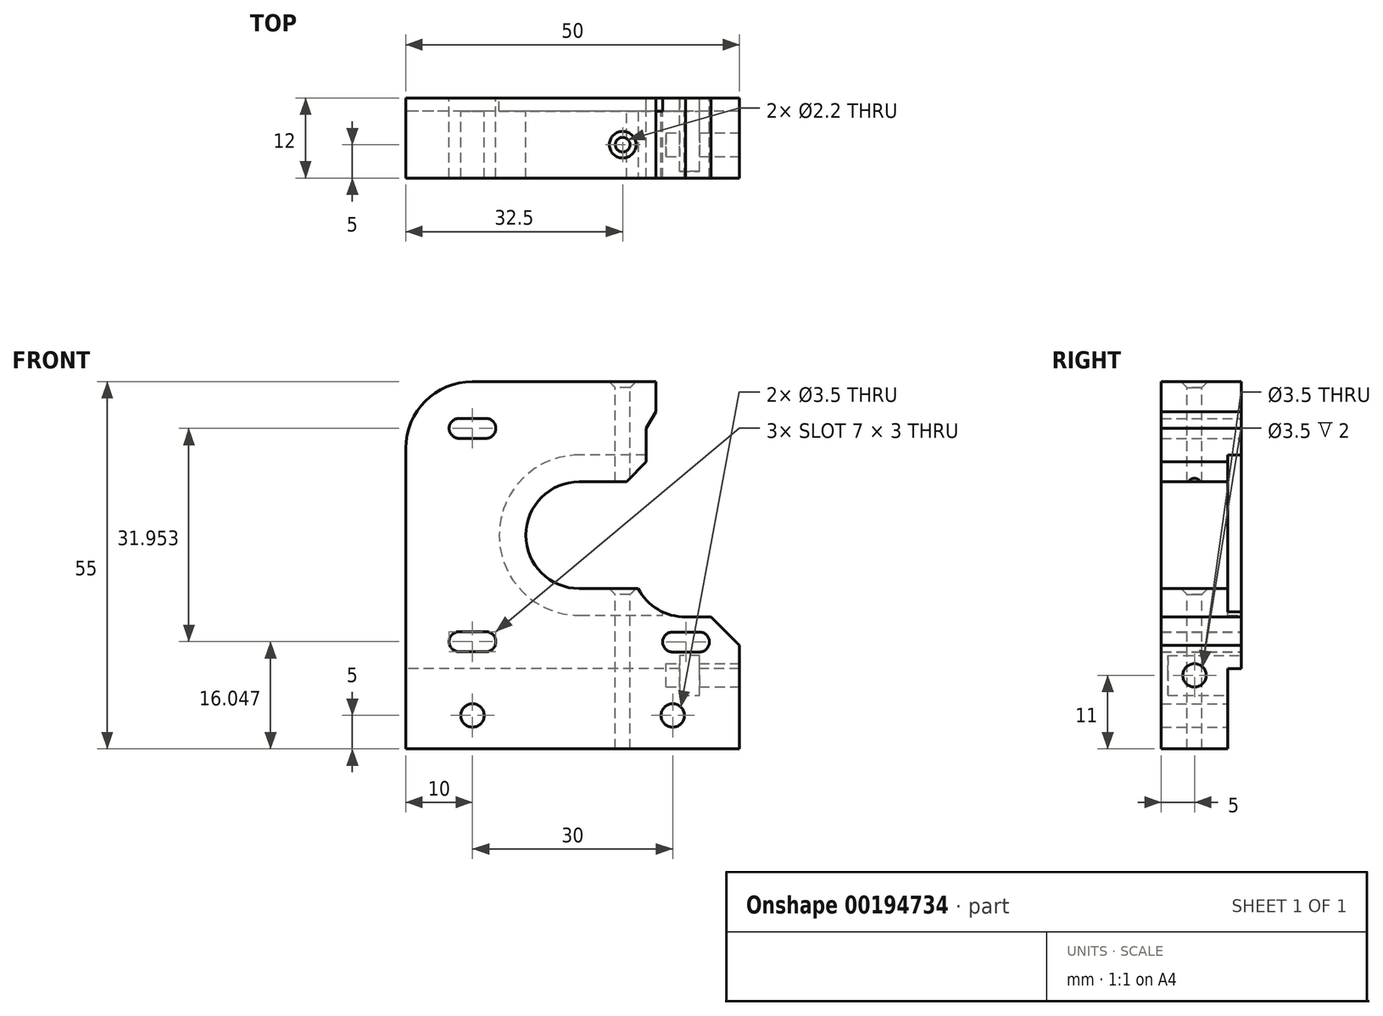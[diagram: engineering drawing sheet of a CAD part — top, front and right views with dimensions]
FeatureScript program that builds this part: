
annotation { "Feature Type Name" : "Feature", "Feature Type Description" : "" }
export const myFeature = defineFeature(function(context is Context, id is Id, definition is map)
    precondition{}
    {
        {
            var Q0;
            Q0=qCreatedBy(makeId("Front.planeOp"),FACE);
            var sketch = newSketch(context, id + "F0", { "sketchPlane" : qUnion([Q0])});
            skLineSegment(sketch, "E0", {"start": v(0, 0) * mm, "end": v(0, 45) * mm});
            skLineSegment(sketch, "E1", {"start": v(10, 55) * mm, "end": v(37.5, 55) * mm});
            skLineSegment(sketch, "E2", {"start": v(50, 15.5) * mm, "end": v(50, 0) * mm});
            skLineSegment(sketch, "E3", {"start": v(50, 0) * mm, "end": v(0, 0) * mm});
            skArc(sketch, "E4", {"start": v(10, 55) * mm, "mid": v(2.93, 52.07) * mm, "end": v(0, 45) * mm});
            skLineSegment(sketch, "E5", {"start": v(10, 67.16) * mm, "end": v(42, 67.16) * mm});
            skLineSegment(sketch, "E6", {"start": v(12, 46.5) * mm, "end": v(8, 46.5) * mm});
            skArc(sketch, "E7", {"start": v(12, 46.5) * mm, "mid": v(13.5, 48) * mm, "end": v(12, 49.5) * mm});
            skArc(sketch, "E8", {"start": v(8, 49.5) * mm, "mid": v(6.5, 48) * mm, "end": v(8, 46.5) * mm});
            skLineSegment(sketch, "E9", {"start": v(8, 49.5) * mm, "end": v(12, 49.5) * mm});
            skLineSegment(sketch, "E10", {"start": v(12, 14.55) * mm, "end": v(8, 14.55) * mm});
            skArc(sketch, "E11", {"start": v(12, 14.55) * mm, "mid": v(13.5, 16.05) * mm, "end": v(12, 17.55) * mm});
            skArc(sketch, "E12", {"start": v(8, 17.55) * mm, "mid": v(6.5, 16.05) * mm, "end": v(8, 14.55) * mm});
            skLineSegment(sketch, "E13", {"start": v(8, 17.55) * mm, "end": v(12, 17.55) * mm});
            skLineSegment(sketch, "E14", {"start": v(44, 14.5) * mm, "end": v(40, 14.5) * mm});
            skArc(sketch, "E15", {"start": v(44, 14.5) * mm, "mid": v(45.5, 16) * mm, "end": v(44, 17.5) * mm});
            skArc(sketch, "E16", {"start": v(40, 17.5) * mm, "mid": v(38.5, 16) * mm, "end": v(40, 14.5) * mm});
            skLineSegment(sketch, "E17", {"start": v(40, 17.5) * mm, "end": v(44, 17.5) * mm});
            skPoint(sketch, "E18.endSnap0", {"position": v(42, 17.5) * mm});
            skArc(sketch, "E19", {"start": v(26, 40) * mm, "mid": v(18, 32) * mm, "end": v(26, 24) * mm});
            skLineSegment(sketch, "E20", {"start": v(26, 24) * mm, "end": v(35, 24) * mm});
            skLineSegment(sketch, "E21", {"start": v(45, 20.5) * mm, "end": v(38.5, 20.5) * mm});
            skLineSegment(sketch, "E22", {"start": v(38.5, 20.5) * mm, "end": v(35, 24) * mm});
            skLineSegment(sketch, "E23", {"start": v(37.5, 55) * mm, "end": v(37.5, 50.5) * mm});
            skLineSegment(sketch, "E24", {"start": v(37.5, 50.5) * mm, "end": v(36, 48) * mm});
            skLineSegment(sketch, "E25", {"start": v(33.1, 40) * mm, "end": v(26, 40) * mm});
            skLineSegment(sketch, "E26", {"start": v(36, 48) * mm, "end": v(36, 43) * mm});
            skLineSegment(sketch, "E27", {"start": v(36, 43) * mm, "end": v(33.1, 40) * mm});
            skCircle(sketch, "E28", {"center": v(10, 5) * mm, "radius": 1.75 * mm});
            skCircle(sketch, "E29", {"center": v(40, 5) * mm, "radius": 1.75 * mm});
            skPoint(sketch, "E30.orphan", {"position": v(0, 55) * mm});
            skLineSegment(sketch, "E31", {"start": v(50, 15.5) * mm, "end": v(45, 20.5) * mm});
            skPoint(sketch, "E32.orphan", {"position": v(50, 20.5) * mm});
            skSolve(sketch);
        }
        {
            var Q0;
            Q0 = qSketchRegion(id + "F0", true);
            extrude(context, id + "F1", {"entities" : qUnion([Q0]), "depth" : 12 * mm});
        }
        {
            var Q0;
            Q0=makeQuery(id+"F1.opExtrude","CAP_FACE",FACE,{"disambiguationData":[OSD([sQuery(id+"F0.wireOp",EDGE,"E0"),sQuery(id+"F0.wireOp",EDGE,"E1"),sQuery(id+"F0.wireOp",EDGE,"E2"),sQuery(id+"F0.wireOp",EDGE,"E3"),sQuery(id+"F0.wireOp",EDGE,"E4"),sQuery(id+"F0.wireOp",EDGE,"E6"),sQuery(id+"F0.wireOp",EDGE,"E7"),sQuery(id+"F0.wireOp",EDGE,"E8"),sQuery(id+"F0.wireOp",EDGE,"E9"),sQuery(id+"F0.wireOp",EDGE,"E10"),sQuery(id+"F0.wireOp",EDGE,"E11"),sQuery(id+"F0.wireOp",EDGE,"E12"),sQuery(id+"F0.wireOp",EDGE,"E13"),sQuery(id+"F0.wireOp",EDGE,"E14"),sQuery(id+"F0.wireOp",EDGE,"E15"),sQuery(id+"F0.wireOp",EDGE,"E16"),sQuery(id+"F0.wireOp",EDGE,"E17"),sQuery(id+"F0.wireOp",EDGE,"E19"),sQuery(id+"F0.wireOp",EDGE,"E20"),sQuery(id+"F0.wireOp",EDGE,"E21"),sQuery(id+"F0.wireOp",EDGE,"E22"),sQuery(id+"F0.wireOp",EDGE,"E23"),sQuery(id+"F0.wireOp",EDGE,"E24"),sQuery(id+"F0.wireOp",EDGE,"E25"),sQuery(id+"F0.wireOp",EDGE,"E26"),sQuery(id+"F0.wireOp",EDGE,"E27"),sQuery(id+"F0.wireOp",EDGE,"E28"),sQuery(id+"F0.wireOp",EDGE,"E29"),sQuery(id+"F0.wireOp",EDGE,"E31")])],"isStart":true});
            var sketch = newSketch(context, id + "F2", { "sketchPlane" : qUnion([Q0])});
            skArc(sketch, "E33", {"start": v(-26.08, 20) * mm, "mid": v(-14, 32) * mm, "end": v(-26.08, 44) * mm});
            skLineSegment(sketch, "E34", {"start": v(-26.08, 44) * mm, "end": v(-36, 44) * mm});
            skLineSegment(sketch, "E35", {"start": v(-26.08, 20) * mm, "end": v(-38.5, 20) * mm});
            skLineSegment(sketch, "E36", {"start": v(-38.5, 20) * mm, "end": v(-38.5, 20.5) * mm});
            skLineSegment(sketch, "E37", {"start": v(-38.5, 20.5) * mm, "end": v(-38.5, 44) * mm});
            skLineSegment(sketch, "E38", {"start": v(-38.5, 44) * mm, "end": v(-36, 44) * mm});
            skSolve(sketch);
        }
        {
            var Q0;
            Q0 = qSketchRegion(id + "F2", true);
            extrude(context, id + "F3", {"entities" : qUnion([Q0]), "operationType" : NewBodyOperationType.REMOVE, "oppositeDirection" : true, "depth" : 2 * mm});
        }
        {
            var Q0;
            Q0=makeQuery(id+"F1.opExtrude","CAP_FACE",FACE,{"disambiguationData":[OSD([sQuery(id+"F0.wireOp",EDGE,"E0"),sQuery(id+"F0.wireOp",EDGE,"E1"),sQuery(id+"F0.wireOp",EDGE,"E2"),sQuery(id+"F0.wireOp",EDGE,"E3"),sQuery(id+"F0.wireOp",EDGE,"E4"),sQuery(id+"F0.wireOp",EDGE,"E6"),sQuery(id+"F0.wireOp",EDGE,"E7"),sQuery(id+"F0.wireOp",EDGE,"E8"),sQuery(id+"F0.wireOp",EDGE,"E9"),sQuery(id+"F0.wireOp",EDGE,"E10"),sQuery(id+"F0.wireOp",EDGE,"E11"),sQuery(id+"F0.wireOp",EDGE,"E12"),sQuery(id+"F0.wireOp",EDGE,"E13"),sQuery(id+"F0.wireOp",EDGE,"E14"),sQuery(id+"F0.wireOp",EDGE,"E15"),sQuery(id+"F0.wireOp",EDGE,"E16"),sQuery(id+"F0.wireOp",EDGE,"E17"),sQuery(id+"F0.wireOp",EDGE,"E19"),sQuery(id+"F0.wireOp",EDGE,"E20"),sQuery(id+"F0.wireOp",EDGE,"E21"),sQuery(id+"F0.wireOp",EDGE,"E22"),sQuery(id+"F0.wireOp",EDGE,"E23"),sQuery(id+"F0.wireOp",EDGE,"E24"),sQuery(id+"F0.wireOp",EDGE,"E25"),sQuery(id+"F0.wireOp",EDGE,"E26"),sQuery(id+"F0.wireOp",EDGE,"E27"),sQuery(id+"F0.wireOp",EDGE,"E28"),sQuery(id+"F0.wireOp",EDGE,"E29"),sQuery(id+"F0.wireOp",EDGE,"E31")])],"isStart":true});
            var sketch = newSketch(context, id + "F4", { "sketchPlane" : qUnion([Q0])});
            skLineSegment(sketch, "E39.bottom", {"start": v(-50, 0) * mm, "end": v(0, 0) * mm});
            skLineSegment(sketch, "E39.top", {"start": v(-50, 12.02) * mm, "end": v(0, 12.02) * mm});
            skLineSegment(sketch, "E39.left", {"start": v(-50, 0) * mm, "end": v(-50, 12.02) * mm});
            skLineSegment(sketch, "E39.right", {"start": v(0, 0) * mm, "end": v(0, 12.02) * mm});
            skSolve(sketch);
        }
        {
            var Q0;
            Q0 = qSketchRegion(id + "F4", true);
            extrude(context, id + "F5", {"entities" : qUnion([Q0]), "operationType" : NewBodyOperationType.REMOVE, "oppositeDirection" : true, "depth" : 2 * mm});
        }
        {
            var Q0;
            Q0=makeQuery(id+"F1.opExtrude","SWEPT_FACE",FACE,{"disambiguationData":[OSD([sQuery(id+"F0.wireOp",EDGE,"E1")])]});
            var sketch = newSketch(context, id + "F6", { "sketchPlane" : qUnion([Q0])});
            skLineSegment(sketch, "E40", {"start": v(41.11, -12) * mm, "end": v(41.11, -7) * mm});
            skLineSegment(sketch, "E41", {"start": v(41.11, -7) * mm, "end": v(37.5, -7) * mm});
            skCircle(sketch, "E42", {"center": v(32.5, -7) * mm, "radius": 1.1 * mm});
            skSolve(sketch);
        }
        {
            var Q0;
            Q0 = qSketchRegion(id + "F6", true);
            extrude(context, id + "F7", {"entities" : qUnion([Q0]), "operationType" : NewBodyOperationType.REMOVE, "oppositeDirection" : true, "depth" : 60 * mm});
        }
        {
            var Q0;
            Q0=makeQuery(id+"F1.opExtrude","SWEPT_FACE",FACE,{"disambiguationData":[OSD([sQuery(id+"F0.wireOp",EDGE,"E2")])]});
            var sketch = newSketch(context, id + "F8", { "sketchPlane" : qUnion([Q0])});
            skLineSegment(sketch, "E43", {"start": v(-7, 0) * mm, "end": v(-7, 11) * mm});
            skCircle(sketch, "E44", {"center": v(-7, 11) * mm, "radius": 1.75 * mm});
            skSolve(sketch);
        }
        {
            var Q0;
            Q0 = qSketchRegion(id + "F8", true);
            extrude(context, id + "F9", {"entities" : qUnion([Q0]), "operationType" : NewBodyOperationType.REMOVE, "oppositeDirection" : true, "depth" : 11 * mm});
        }
        {
            var Q0;
            Q0=makeQuery(id+"F1.opExtrude","CAP_FACE",FACE,{"disambiguationData":[OSD([sQuery(id+"F0.wireOp",EDGE,"E0"),sQuery(id+"F0.wireOp",EDGE,"E1"),sQuery(id+"F0.wireOp",EDGE,"E2"),sQuery(id+"F0.wireOp",EDGE,"E3"),sQuery(id+"F0.wireOp",EDGE,"E4"),sQuery(id+"F0.wireOp",EDGE,"E6"),sQuery(id+"F0.wireOp",EDGE,"E7"),sQuery(id+"F0.wireOp",EDGE,"E8"),sQuery(id+"F0.wireOp",EDGE,"E9"),sQuery(id+"F0.wireOp",EDGE,"E10"),sQuery(id+"F0.wireOp",EDGE,"E11"),sQuery(id+"F0.wireOp",EDGE,"E12"),sQuery(id+"F0.wireOp",EDGE,"E13"),sQuery(id+"F0.wireOp",EDGE,"E14"),sQuery(id+"F0.wireOp",EDGE,"E15"),sQuery(id+"F0.wireOp",EDGE,"E16"),sQuery(id+"F0.wireOp",EDGE,"E17"),sQuery(id+"F0.wireOp",EDGE,"E19"),sQuery(id+"F0.wireOp",EDGE,"E20"),sQuery(id+"F0.wireOp",EDGE,"E21"),sQuery(id+"F0.wireOp",EDGE,"E22"),sQuery(id+"F0.wireOp",EDGE,"E23"),sQuery(id+"F0.wireOp",EDGE,"E24"),sQuery(id+"F0.wireOp",EDGE,"E25"),sQuery(id+"F0.wireOp",EDGE,"E26"),sQuery(id+"F0.wireOp",EDGE,"E27"),sQuery(id+"F0.wireOp",EDGE,"E28"),sQuery(id+"F0.wireOp",EDGE,"E29"),sQuery(id+"F0.wireOp",EDGE,"E31")])],"isStart":true});
            var sketch = newSketch(context, id + "F10", { "sketchPlane" : qUnion([Q0])});
            skLineSegment(sketch, "E45", {"start": v(-44, 11) * mm, "end": v(-44, 14) * mm});
            skLineSegment(sketch, "E46", {"start": v(-44, 14) * mm, "end": v(-41, 14) * mm});
            skLineSegment(sketch, "E47", {"start": v(-41, 14) * mm, "end": v(-41, 8) * mm});
            skLineSegment(sketch, "E48", {"start": v(-41, 8) * mm, "end": v(-44, 8) * mm});
            skLineSegment(sketch, "E49", {"start": v(-44, 8) * mm, "end": v(-44, 11) * mm});
            skSolve(sketch);
        }
        {
            var Q0;
            Q0 = qSketchRegion(id + "F10", true);
            extrude(context, id + "F11", {"entities" : qUnion([Q0]), "operationType" : NewBodyOperationType.REMOVE, "oppositeDirection" : true, "depth" : 11 * mm});
        }
        {
            var Q0;
            Q0=makeQuery(id+"F1.opExtrude","SWEPT_FACE",FACE,{"disambiguationData":[OSD([sQuery(id+"F0.wireOp",EDGE,"E20")])]});
            var sketch = newSketch(context, id + "F12", { "sketchPlane" : qUnion([Q0])});
            skLineSegment(sketch, "E50", {"start": v(35, -12) * mm, "end": v(35, -7) * mm});
            skLineSegment(sketch, "E51", {"start": v(35, -7) * mm, "end": v(32.5, -7) * mm});
            skSolve(sketch);
        }
        {
            var Q0;
            Q0=sQuery(id+"F12.wireOp",VERTEX,"E51.end");
            var Q1;
            Q1=makeQuery(id+"F1.opExtrude","SWEPT_BODY",BODY,{"disambiguationData":[OSD([sQuery(id+"F0.wireOp",EDGE,"E0"),sQuery(id+"F0.wireOp",EDGE,"E1"),sQuery(id+"F0.wireOp",EDGE,"E2"),sQuery(id+"F0.wireOp",EDGE,"E3"),sQuery(id+"F0.wireOp",EDGE,"E4"),sQuery(id+"F0.wireOp",EDGE,"E6"),sQuery(id+"F0.wireOp",EDGE,"E7"),sQuery(id+"F0.wireOp",EDGE,"E8"),sQuery(id+"F0.wireOp",EDGE,"E9"),sQuery(id+"F0.wireOp",EDGE,"E10"),sQuery(id+"F0.wireOp",EDGE,"E11"),sQuery(id+"F0.wireOp",EDGE,"E12"),sQuery(id+"F0.wireOp",EDGE,"E13"),sQuery(id+"F0.wireOp",EDGE,"E14"),sQuery(id+"F0.wireOp",EDGE,"E15"),sQuery(id+"F0.wireOp",EDGE,"E16"),sQuery(id+"F0.wireOp",EDGE,"E17"),sQuery(id+"F0.wireOp",EDGE,"E19"),sQuery(id+"F0.wireOp",EDGE,"E20"),sQuery(id+"F0.wireOp",EDGE,"E21"),sQuery(id+"F0.wireOp",EDGE,"E22"),sQuery(id+"F0.wireOp",EDGE,"E23"),sQuery(id+"F0.wireOp",EDGE,"E24"),sQuery(id+"F0.wireOp",EDGE,"E25"),sQuery(id+"F0.wireOp",EDGE,"E26"),sQuery(id+"F0.wireOp",EDGE,"E27"),sQuery(id+"F0.wireOp",EDGE,"E28"),sQuery(id+"F0.wireOp",EDGE,"E29"),sQuery(id+"F0.wireOp",EDGE,"E31")])]});
            hole(context, id + "F13", {"style" : HoleStyle.C_SINK, "endStyle" : HoleEndStyle.BLIND, "holeDiameter" : 2.2 * mm, "cSinkDiameter" : 4 * mm, "cSinkAngle" : 90 * degree, "holeDepth" : 3 * mm, "isTappedThrough" : true, "tappedDepth" : 12 * mm, "tapClearance" : 3, "startFromSketch" : true, "locations" : qUnion([Q0]), "scope" : qUnion([Q1])});
        }
        {
            var Q0;
            Q0=makeQuery(id+"F1.opExtrude","SWEPT_FACE",FACE,{"disambiguationData":[OSD([sQuery(id+"F0.wireOp",EDGE,"E1")])]});
            var sketch = newSketch(context, id + "F14", { "sketchPlane" : qUnion([Q0])});
            skLineSegment(sketch, "E52", {"start": v(37.5, -12) * mm, "end": v(32.5, -7) * mm});
            skSolve(sketch);
        }
        {
            var Q0;
            Q0=sQuery(id+"F14.wireOp",VERTEX,"E52.end");
            var Q1;
            Q1=makeQuery(id+"F1.opExtrude","SWEPT_BODY",BODY,{"disambiguationData":[OSD([sQuery(id+"F0.wireOp",EDGE,"E0"),sQuery(id+"F0.wireOp",EDGE,"E1"),sQuery(id+"F0.wireOp",EDGE,"E2"),sQuery(id+"F0.wireOp",EDGE,"E3"),sQuery(id+"F0.wireOp",EDGE,"E4"),sQuery(id+"F0.wireOp",EDGE,"E6"),sQuery(id+"F0.wireOp",EDGE,"E7"),sQuery(id+"F0.wireOp",EDGE,"E8"),sQuery(id+"F0.wireOp",EDGE,"E9"),sQuery(id+"F0.wireOp",EDGE,"E10"),sQuery(id+"F0.wireOp",EDGE,"E11"),sQuery(id+"F0.wireOp",EDGE,"E12"),sQuery(id+"F0.wireOp",EDGE,"E13"),sQuery(id+"F0.wireOp",EDGE,"E14"),sQuery(id+"F0.wireOp",EDGE,"E15"),sQuery(id+"F0.wireOp",EDGE,"E16"),sQuery(id+"F0.wireOp",EDGE,"E17"),sQuery(id+"F0.wireOp",EDGE,"E19"),sQuery(id+"F0.wireOp",EDGE,"E20"),sQuery(id+"F0.wireOp",EDGE,"E21"),sQuery(id+"F0.wireOp",EDGE,"E22"),sQuery(id+"F0.wireOp",EDGE,"E23"),sQuery(id+"F0.wireOp",EDGE,"E24"),sQuery(id+"F0.wireOp",EDGE,"E25"),sQuery(id+"F0.wireOp",EDGE,"E26"),sQuery(id+"F0.wireOp",EDGE,"E27"),sQuery(id+"F0.wireOp",EDGE,"E28"),sQuery(id+"F0.wireOp",EDGE,"E29"),sQuery(id+"F0.wireOp",EDGE,"E31")])]});
            hole(context, id + "F15", {"style" : HoleStyle.C_SINK, "endStyle" : HoleEndStyle.BLIND, "holeDiameter" : 2.2 * mm, "cSinkDiameter" : 4 * mm, "cSinkAngle" : 90 * degree, "holeDepth" : 3 * mm, "isTappedThrough" : true, "tappedDepth" : 12 * mm, "tapClearance" : 3, "startFromSketch" : true, "locations" : qUnion([Q0]), "scope" : qUnion([Q1])});
        }
        {
            var Q0;
            Q0=makeQuery(id+"F1.opExtrude","CAP_FACE",FACE,{"disambiguationData":[OSD([sQuery(id+"F0.wireOp",EDGE,"E0"),sQuery(id+"F0.wireOp",EDGE,"E1"),sQuery(id+"F0.wireOp",EDGE,"E2"),sQuery(id+"F0.wireOp",EDGE,"E3"),sQuery(id+"F0.wireOp",EDGE,"E4"),sQuery(id+"F0.wireOp",EDGE,"E6"),sQuery(id+"F0.wireOp",EDGE,"E7"),sQuery(id+"F0.wireOp",EDGE,"E8"),sQuery(id+"F0.wireOp",EDGE,"E9"),sQuery(id+"F0.wireOp",EDGE,"E10"),sQuery(id+"F0.wireOp",EDGE,"E11"),sQuery(id+"F0.wireOp",EDGE,"E12"),sQuery(id+"F0.wireOp",EDGE,"E13"),sQuery(id+"F0.wireOp",EDGE,"E14"),sQuery(id+"F0.wireOp",EDGE,"E15"),sQuery(id+"F0.wireOp",EDGE,"E16"),sQuery(id+"F0.wireOp",EDGE,"E17"),sQuery(id+"F0.wireOp",EDGE,"E19"),sQuery(id+"F0.wireOp",EDGE,"E20"),sQuery(id+"F0.wireOp",EDGE,"E21"),sQuery(id+"F0.wireOp",EDGE,"E22"),sQuery(id+"F0.wireOp",EDGE,"E23"),sQuery(id+"F0.wireOp",EDGE,"E24"),sQuery(id+"F0.wireOp",EDGE,"E25"),sQuery(id+"F0.wireOp",EDGE,"E26"),sQuery(id+"F0.wireOp",EDGE,"E27"),sQuery(id+"F0.wireOp",EDGE,"E28"),sQuery(id+"F0.wireOp",EDGE,"E29"),sQuery(id+"F0.wireOp",EDGE,"E31")])],"isStart":false});
            var sketch = newSketch(context, id + "F16", { "sketchPlane" : qUnion([Q0])});
            skArc(sketch, "E53", {"start": v(45.72, 20.86) * mm, "mid": v(39.62, 35.09) * mm, "end": v(41.94, 19.78) * mm});
            skLineSegment(sketch, "E54", {"start": v(41.57, 19.78) * mm, "end": v(45.72, 19.78) * mm});
            skLineSegment(sketch, "E55", {"start": v(45.72, 19.78) * mm, "end": v(45.72, 20.86) * mm});
            skSolve(sketch);
        }
        {
            var Q0;
            Q0 = qSketchRegion(id + "F16", true);
            extrude(context, id + "F17", {"entities" : qUnion([Q0]), "operationType" : NewBodyOperationType.REMOVE, "oppositeDirection" : true, "depth" : 25 * mm});
        }
    });
